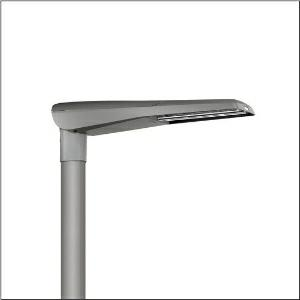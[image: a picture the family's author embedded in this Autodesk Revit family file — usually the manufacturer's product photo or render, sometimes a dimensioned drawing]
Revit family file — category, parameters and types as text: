
# Revit family: streetlight_sl_11_iq_mini___pc-l_5xc2ec1f08he_97a8
name_source: partatom
category: Lighting Fixtures
units: mm (PartAtom-declared; Revit-internal decimal feet)

## family parameters
Cut with Voids When Loaded = No
Host = Face
Light Source = No
Part Type = Normal
Room Calculation Point = No
Round Connector Dimension = Use Diameter
Shared = No

## types (1)
- --- (1 x LED, 5820 lm, 63.6 W, 2200K)
    Apparent Load = 64 VA
    CIE Flux Codes = 37 73 96 100 100
    Color Rendering = 70
    Color Temperature = 2200K
    Default Elevation = 1800 mm
    Description = Streetlight SL 11 iQ mini, mast luminaire, primary light control with 3 zone facetted reflector, of plastic, silver coated, highly specular, primary optical cover: cover, of PMMA, transparent, light distribution: PC-L, light emission: direct distribution, primary light characteristic: asymmetric, left, installation type: post-top, side-entry, LED, High Power LED, rated luminous flux: 7.110lm, luminous efficacy: 114lm/W, light colour: 722/727/730/740, colour temperature: 2200/2700/3000/4000K, control gear: iQ Street-Remote, control: Street-Remote, Auto-Match, Temp-Guard, Lumen-Switch, Night-Set, Smart-Wire, Light-Fading, Desk-Remote (wireless, voltage-free reading and setting of iQ features in the workshop via application-optimized NFC function/RFID function), optimised constant luminous flux control (CLO 2.0), with cable H07RN-F 5x 1.5mm², mains connection: 230..240V, AC, 50/60Hz, connection cable pre-assembled, cable length: 8,5m, start of lifetime: 62W, end of service life: 66W, reduction: 29W, luminaire housing, of diecast aluminium, powder-coated, Siteco® metallic grey (DB 702S), please order mast flange separately, inclination adjustable without tools: 0°, 5°, 10°, 15° (post-top) | 0°, -5°, -10°, -15° (side-entry), sealing non-destructively replaceable, multi-level sealing system, length: 736mm, width: 174mm, height: 116mm, mast flange for spigot size: 42mm (side-entry): 5XC10008XM4, 60/48mm (side-entry/post-top): 5XC10108XM2, 76/60mm (side-entry/post-top): 5XC10108XM1, mounting height: 4..8m, equipment: Power, protection rating (complete): IP66, insulation class (complete): insulation class II (safety insulation), certification: CE, ENEC, VDE, impact resistance: IK09, permissible operating ambient temperature for outdoor applications: -25..+50°C, standard-compliant lighting for roads and squares, Environmental Product Declaration (EPD) tested and certified by an independent institute, packaging unit: 1 piece

Light Distribution: PC-L
    Height = 116 mm
    Lamp = 1 x LED
    Lamp Light Flux = 5820 lm
    Lamp Power = 63.6 W
    Lamp count = 1
    Length = 736 mm
    Luminous efficacy = 92 lm/W
    Manufacturer = Siteco
    ModVariant = No
    Model = 5XC2EC1F08HE
    Number of Poles = 1
    OnlyDefault = Yes
    Power Factor = 1
    Product Name = Streetlight SL 11 iQ mini | PC-L
    Product group = mast luminaire | pylon top
    ProductGroupID = 6100
    Protection Class = Protection class II
    Protection Degree = IP 66
    RLX_Detail_Level = 1
    RLX_Emergency_Light_Flux = 0 lm
    RLX_Emergency_Type = 0
    RLX_Emergency_Type_DB = No
    RlxData = <blob elided: 57285 chars, md5=b7404852>
    Socket = socket
    Standby Power = 0 W
    System Light Flux = 5820 lm
    System Power = 64 W
    Type Comments = individual setting: luminous flux: 100 % | dim-lin: 254 | 866 mA
    Type Image = l_1003508.jpg
    URL = http://relux.com
    VarID = @adj_029178
    Voltage = 0 V
    Weight = 0.00 kg
    Width = 174 mm

## geometry (parser evidence)
native form markers: Blend x4, Sweep x12
no freeform markers — native parametric forms only
